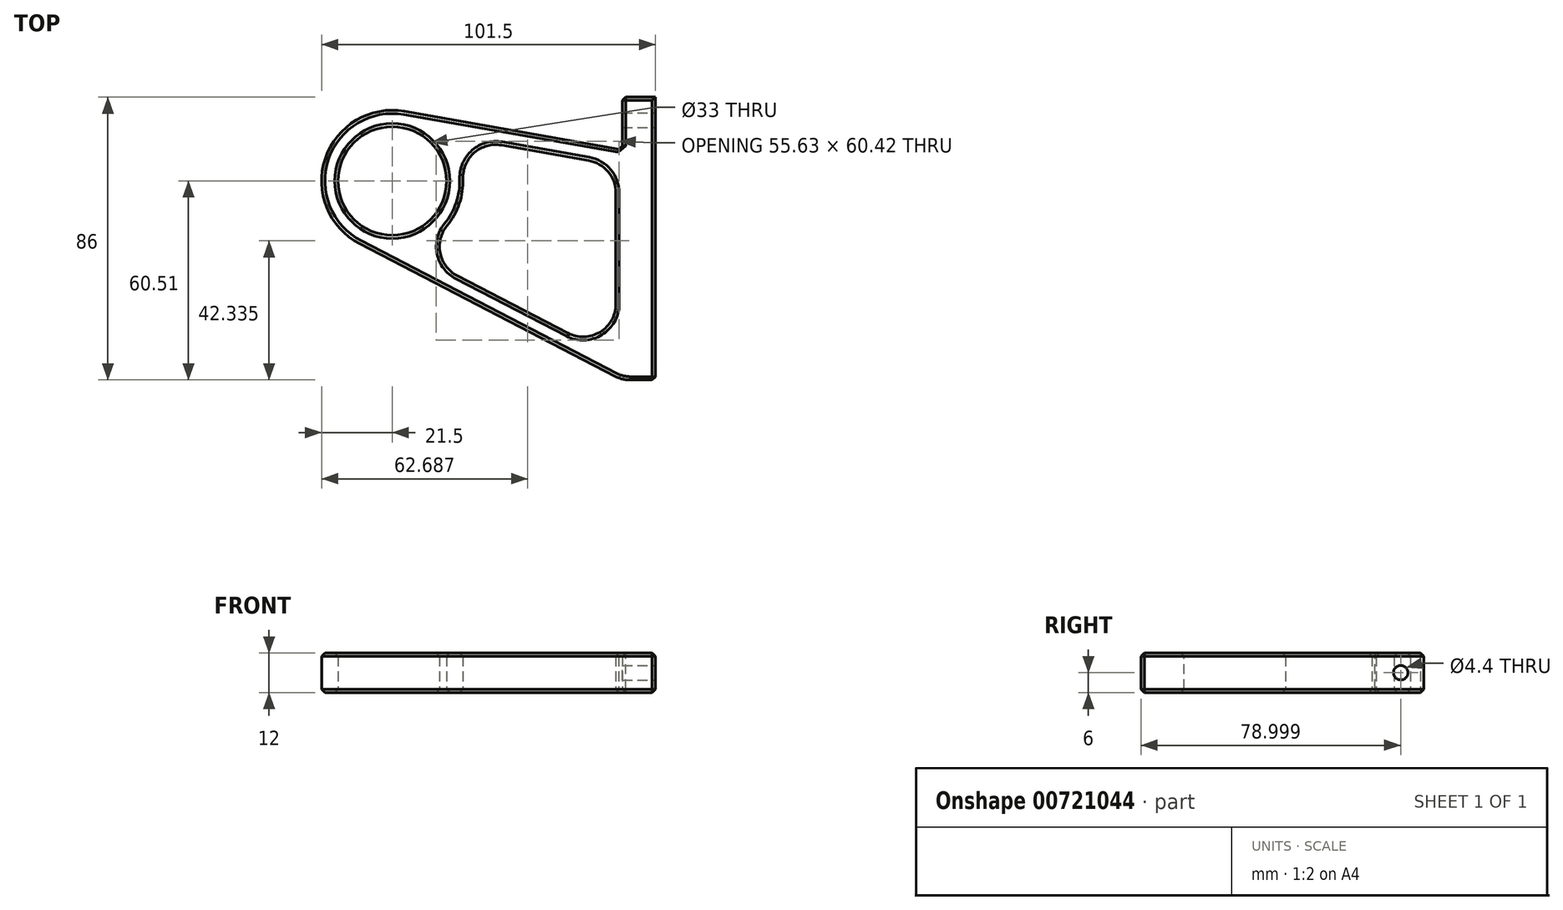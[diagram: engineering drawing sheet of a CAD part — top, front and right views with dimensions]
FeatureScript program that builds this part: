
annotation { "Feature Type Name" : "Feature", "Feature Type Description" : "" }
export const myFeature = defineFeature(function(context is Context, id is Id, definition is map)
    precondition{}
    {
        {
            var Q0;
            Q0=qCreatedBy(makeId("Top.planeOp"),FACE);
            var sketch = newSketch(context, id + "F0", { "sketchPlane" : qUnion([Q0])});
            skCircle(sketch, "E0", {"center": v(0, 0) * mm, "radius": 16.5 * mm});
            skArc(sketch, "E1", {"start": v(3.73, 21.17) * mm, "mid": v(-20.36, 6.9) * mm, "end": v(-9.9, -19.09) * mm});
            skLineSegment(sketch, "E2", {"start": v(70, 25.49) * mm, "end": v(70, 9.49) * mm});
            skLineSegment(sketch, "E3", {"start": v(70, 9.49) * mm, "end": v(3.73, 21.17) * mm});
            skLineSegment(sketch, "E4", {"start": v(-9.9, -19.09) * mm, "end": v(70, -60.51) * mm});
            skLineSegment(sketch, "E5", {"start": v(70, 9.49) * mm, "end": v(70, -60.51) * mm, "construction": true});
            skLineSegment(sketch, "E6", {"start": v(70, 25.49) * mm, "end": v(80, 25.49) * mm});
            skLineSegment(sketch, "E7", {"start": v(80, 25.49) * mm, "end": v(80, -60.51) * mm});
            skLineSegment(sketch, "E8", {"start": v(80, -60.51) * mm, "end": v(70, -60.51) * mm});
            skLineSegment(sketch, "E9", {"start": v(16.44, 13.86) * mm, "end": v(68, 4.76) * mm});
            skLineSegment(sketch, "E10", {"start": v(68, 4.76) * mm, "end": v(68, -53.84) * mm});
            skLineSegment(sketch, "E11", {"start": v(68, -53.84) * mm, "end": v(4.64, -21) * mm});
            skArc(sketch, "E12", {"start": v(16.44, 13.86) * mm, "mid": v(20.36, -6.9) * mm, "end": v(4.64, -21) * mm});
            skSolve(sketch);
        }
        {
            var Q0;
            Q0=makeQuery(id+"F0.imprint","IMPRINT",FACE,{"disambiguationData":[TD([[makeQuery(id+"F0.imprint","IMPRINT",EDGE,{"derivedFrom":sQuery(id+"F0.wireOp",EDGE,"E0")}),-1.0]])]});
            extrude(context, id + "F1", {"entities" : qUnion([Q0]), "depth" : 12 * mm, "offsetDistance" : 25 * mm, "symmetric" : true});
        }
        {
            var Q0;
            Q0=makeQuery(id+"F1.opExtrude","SWEPT_EDGE",EDGE,{"disambiguationData":[OSD([sQuery(id+"F0.wireOp",EDGE,"E9"),sQuery(id+"F0.wireOp",EDGE,"E10")])]});
            var Q1;
            Q1=makeQuery(id+"F1.opExtrude","SWEPT_EDGE",EDGE,{"disambiguationData":[OSD([sQuery(id+"F0.wireOp",EDGE,"E10"),sQuery(id+"F0.wireOp",EDGE,"E11")])]});
            var Q2;
            Q2=makeQuery(id+"F1.opExtrude","SWEPT_EDGE",EDGE,{"disambiguationData":[OSD([sQuery(id+"F0.wireOp",EDGE,"E4"),sQuery(id+"F0.wireOp",EDGE,"fd981aa8-1bd8-448a-9d14-09a27edd32ea")])]});
            var Q3;
            Q3=makeQuery(id+"F1.opExtrude","SWEPT_EDGE",EDGE,{"disambiguationData":[OSD([sQuery(id+"F0.wireOp",EDGE,"E9"),sQuery(id+"F0.wireOp",EDGE,"E12")])]});
            var Q4;
            Q4=makeQuery(id+"F1.opExtrude","SWEPT_EDGE",EDGE,{"disambiguationData":[OSD([sQuery(id+"F0.wireOp",EDGE,"E11"),sQuery(id+"F0.wireOp",EDGE,"E12")])]});
            fillet(context, id + "F2", {"entities" : qUnion([Q0, Q1, Q2, Q3, Q4]), "radius" : 10 * mm, "tangentPropagation" : true, "allowEdgeOverflow" : false});
        }
        {
            var Q0;
            Q0=makeQuery(id+"F1.opExtrude","CAP_EDGE",EDGE,{"disambiguationData":[OSD([sQuery(id+"F0.wireOp",EDGE,"E0")])],"isStart":false});
            var Q1;
            Q1=makeQuery(id+"F1.opExtrude","CAP_EDGE",EDGE,{"disambiguationData":[OSD([sQuery(id+"F0.wireOp",EDGE,"E0")])],"isStart":true});
            var Q2;
            Q2=makeQuery(id+"F1.opExtrude","CAP_FACE",FACE,{"disambiguationData":[OSD([sQuery(id+"F0.wireOp",EDGE,"E0"),sQuery(id+"F0.wireOp",EDGE,"E1"),sQuery(id+"F0.wireOp",EDGE,"E2"),sQuery(id+"F0.wireOp",EDGE,"E3"),sQuery(id+"F0.wireOp",EDGE,"E4"),sQuery(id+"F0.wireOp",EDGE,"fd981aa8-1bd8-448a-9d14-09a27edd32ea"),sQuery(id+"F0.wireOp",EDGE,"E6"),sQuery(id+"F0.wireOp",EDGE,"E7"),sQuery(id+"F0.wireOp",EDGE,"E8"),sQuery(id+"F0.wireOp",EDGE,"E9"),sQuery(id+"F0.wireOp",EDGE,"E10"),sQuery(id+"F0.wireOp",EDGE,"E11"),sQuery(id+"F0.wireOp",EDGE,"E12")])],"isStart":false});
            var Q3;
            Q3=makeQuery(id+"F1.opExtrude","CAP_FACE",FACE,{"disambiguationData":[OSD([sQuery(id+"F0.wireOp",EDGE,"E0"),sQuery(id+"F0.wireOp",EDGE,"E1"),sQuery(id+"F0.wireOp",EDGE,"E2"),sQuery(id+"F0.wireOp",EDGE,"E3"),sQuery(id+"F0.wireOp",EDGE,"E4"),sQuery(id+"F0.wireOp",EDGE,"fd981aa8-1bd8-448a-9d14-09a27edd32ea"),sQuery(id+"F0.wireOp",EDGE,"E6"),sQuery(id+"F0.wireOp",EDGE,"E7"),sQuery(id+"F0.wireOp",EDGE,"E8"),sQuery(id+"F0.wireOp",EDGE,"E9"),sQuery(id+"F0.wireOp",EDGE,"E10"),sQuery(id+"F0.wireOp",EDGE,"E11"),sQuery(id+"F0.wireOp",EDGE,"E12")])],"isStart":true});
            var Q4;
            Q4=makeQuery(id+"F1.opExtrude","SWEPT_EDGE",EDGE,{"disambiguationData":[OSD([sQuery(id+"F0.wireOp",EDGE,"E2"),sQuery(id+"F0.wireOp",EDGE,"E3")])]});
            var Q5;
            Q5=makeQuery(id+"F1.opExtrude","SWEPT_EDGE",EDGE,{"disambiguationData":[OSD([sQuery(id+"F0.wireOp",EDGE,"E2"),sQuery(id+"F0.wireOp",EDGE,"E6")])]});
            var Q6;
            Q6=makeQuery(id+"F1.opExtrude","SWEPT_EDGE",EDGE,{"disambiguationData":[OSD([sQuery(id+"F0.wireOp",EDGE,"fd981aa8-1bd8-448a-9d14-09a27edd32ea"),sQuery(id+"F0.wireOp",EDGE,"E8")])]});
            chamfer(context, id + "F3", {"entities" : qUnion([Q0, Q1, Q2, Q3, Q4, Q5, Q6]), "width" : 1 * mm, "tangentPropagation" : true});
        }
        {
            var Q0;
            Q0=makeQuery(id+"F1.opExtrude","SWEPT_FACE",FACE,{"disambiguationData":[OSD([sQuery(id+"F0.wireOp",EDGE,"E2")])]});
            var sketch = newSketch(context, id + "F4", { "sketchPlane" : qUnion([Q0])});
            skPoint(sketch, "E13", {"position": v(-18.49, 0) * mm});
            skSolve(sketch);
        }
        {
            var Q0;
            Q0=sQuery(id+"F4.wireOp",VERTEX,"E13");
            var Q1;
            Q1=makeQuery(id+"F1.opExtrude","SWEPT_BODY",BODY,{"disambiguationData":[OSD([sQuery(id+"F0.wireOp",EDGE,"E0"),sQuery(id+"F0.wireOp",EDGE,"E1"),sQuery(id+"F0.wireOp",EDGE,"E2"),sQuery(id+"F0.wireOp",EDGE,"E3"),sQuery(id+"F0.wireOp",EDGE,"E4"),sQuery(id+"F0.wireOp",EDGE,"fd981aa8-1bd8-448a-9d14-09a27edd32ea"),sQuery(id+"F0.wireOp",EDGE,"E6"),sQuery(id+"F0.wireOp",EDGE,"E7"),sQuery(id+"F0.wireOp",EDGE,"E8"),sQuery(id+"F0.wireOp",EDGE,"E9"),sQuery(id+"F0.wireOp",EDGE,"E10"),sQuery(id+"F0.wireOp",EDGE,"E11"),sQuery(id+"F0.wireOp",EDGE,"E12")])]});
            hole(context, id + "F5", {"style" : HoleStyle.SIMPLE, "endStyle" : HoleEndStyle.BLIND, "holeDiameter" : 4.4 * mm, "majorDiameter" : 5 * mm, "holeDepth" : 15 * mm, "isTappedThrough" : true, "tappedDepth" : 12 * mm, "tapClearance" : 3, "locations" : qUnion([Q0]), "scope" : qUnion([Q1])});
        }
    });
